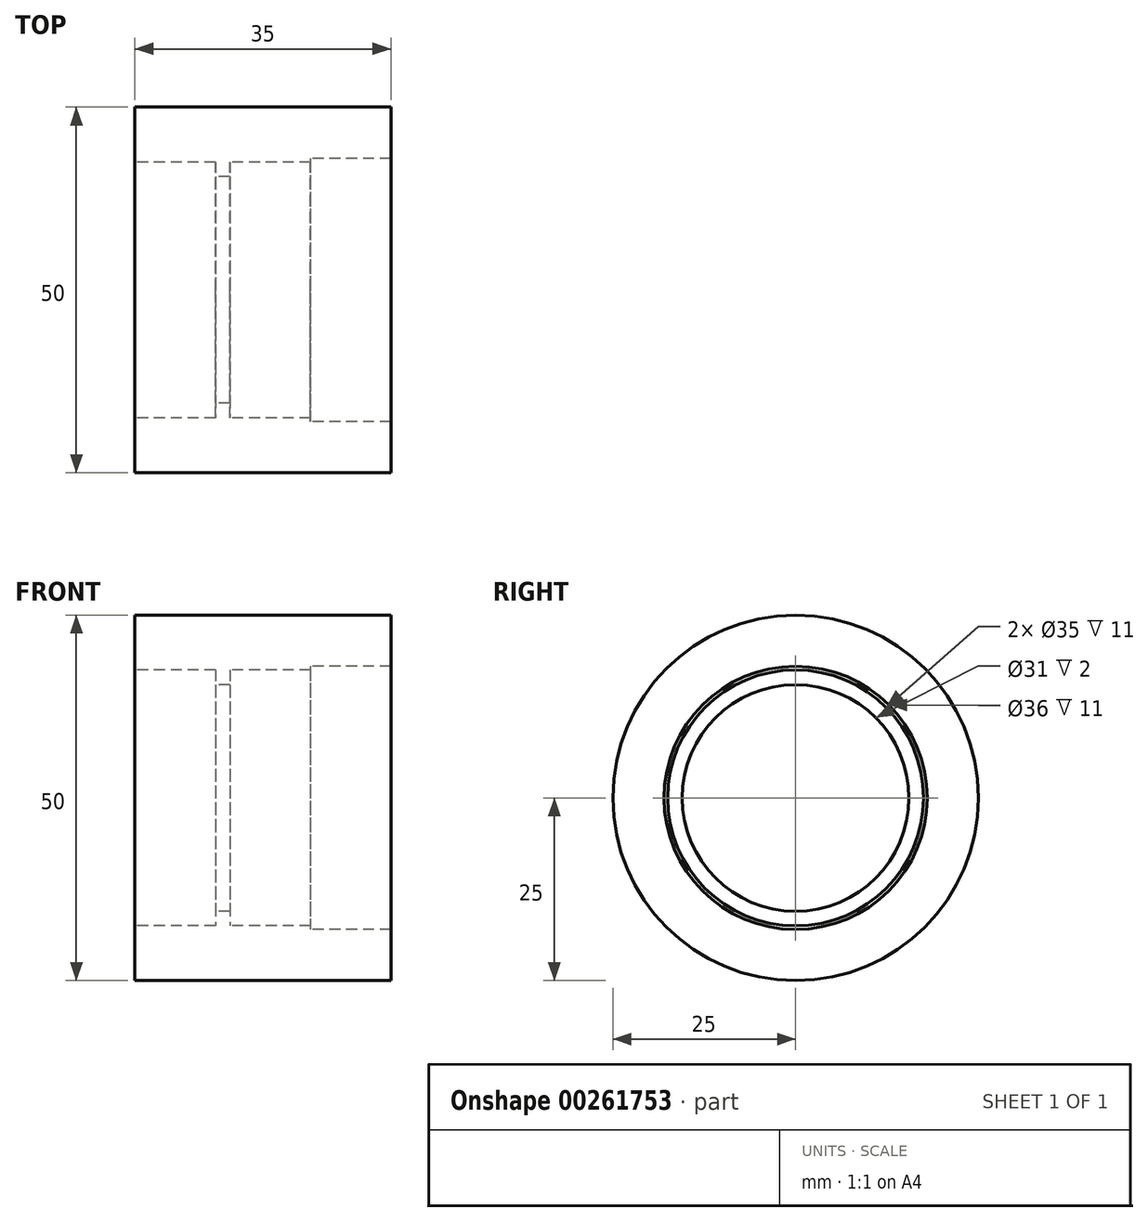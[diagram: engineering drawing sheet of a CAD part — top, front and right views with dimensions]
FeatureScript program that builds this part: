
annotation { "Feature Type Name" : "Feature", "Feature Type Description" : "" }
export const myFeature = defineFeature(function(context is Context, id is Id, definition is map)
    precondition{}
    {
        {
            var Q0;
            Q0=qCreatedBy(makeId("Front.planeOp"),FACE);
            var sketch = newSketch(context, id + "F0", { "sketchPlane" : qUnion([Q0])});
            skLineSegment(sketch, "E0", {"start": v(-14.7, 25) * mm, "end": v(20.3, 25) * mm});
            skLineSegment(sketch, "E1", {"start": v(20.3, 25) * mm, "end": v(20.3, 18) * mm});
            skLineSegment(sketch, "E2", {"start": v(20.3, 18) * mm, "end": v(9.3, 18) * mm});
            skLineSegment(sketch, "E3", {"start": v(9.3, 18) * mm, "end": v(9.3, 17.5) * mm});
            skLineSegment(sketch, "E4", {"start": v(9.3, 17.5) * mm, "end": v(-1.7, 17.5) * mm});
            skLineSegment(sketch, "E5", {"start": v(-1.7, 17.5) * mm, "end": v(-1.7, 15.5) * mm});
            skLineSegment(sketch, "E6", {"start": v(-1.7, 15.5) * mm, "end": v(-3.7, 15.5) * mm});
            skLineSegment(sketch, "E7", {"start": v(-3.7, 15.5) * mm, "end": v(-3.7, 17.5) * mm});
            skLineSegment(sketch, "E8", {"start": v(-3.7, 17.5) * mm, "end": v(-14.7, 17.5) * mm});
            skLineSegment(sketch, "E9", {"start": v(-14.7, 17.5) * mm, "end": v(-14.7, 25) * mm});
            skLineSegment(sketch, "E10", {"start": v(-42.33, 0) * mm, "end": v(43.57, 0) * mm, "construction": true});
            skSolve(sketch);
        }
        {
            var Q0;
            Q0=makeQuery(id+"F0.imprint","IMPRINT",FACE,{"disambiguationData":[TD([[makeQuery(id+"F0.imprint","IMPRINT",EDGE,{"derivedFrom":sQuery(id+"F0.wireOp",EDGE,"E0")}),-1.0]])]});
            var Q1;
            Q1=sQuery(id+"F0.wireOp",EDGE,"E10");
            revolve(context, id + "F1", {"entities" : qUnion([Q0]), "axis" : qUnion([Q1]), "revolveType" : RevolveType.FULL});
        }
    });
